# Revit family: Rohrschellen Form A, Typ TGA, Gummi
name_source: partatom
category: HLS-Bauteile
revit_build: Autodesk Revit 2017 (Build: 20190507_1515(x64)
units: mm (PartAtom-declared; Revit-internal decimal feet)

## family parameters
Arbeitsebenenbasiert = Ja
Beim Laden mit Abzugskörper schneiden = Nein
Bemaßung runder Anschluss = Durchmesser verwenden
Gemeinsam genutzt = Ja
Immer vertikal = Nein
Raumberechnungspunkt = Nein
Teiletyp = Normal

## types (17) — shared parameters
Anschluss = ohne Anschluss
Bauart = zweiteilig
Baustoffklasse = B2
DS = 8 mm  [stored 0.0262467 ft]
Fabrikat = MEFA
Firma = MEFA Befestigungs- und Montagesysteme GmbH
Material = Stahl
Mengeneinheit = St
Oberflaeche = galvanisch verzinkt
Rohraußendurchmesser Zoll = Zoll
Vorgabe-Ansicht = 1219 mm
max. Temperaturbeständigkeit = 100 °C
max. zul. Last horizontal = 0.00 kN
max. zul. Last vertikal = 0.00 kN
vpe = 1 St
zero-valued in all types: AB, HGA, Nennweite DN Rohr, Stärke Material, max. Rohraußendurchmesser, min. Rohraußendurchmesser

## per-type parameters (varying)
| type | A | Achsabstand | Artikelnummer | B | C | D | D0 | DF1 | DF2 | DVS | EAN | Gewicht | Gewicht pro Bauteil | H | Kurztext1 | Kurztext2 | MB | MD | Materialmaße | R | RM | Rohraußendurchmesser | S | Verschluss-Schraube |
| Rohrschellen Form A, Typ TGA, Ø 219, Gummi | 14 mm  [stored 0.0459318 ft] | 304 mm | 109gfba0219 | 357 mm | 24 mm  [stored 0.0787402 ft] | 219 mm  [stored 0.718504 ft] | 235 mm | 48 mm  [stored 0.15748 ft] | 45 mm  [stored 0.147638 ft] | 17 mm | 4250928423672 | 3.27 kg | 3.27 kg | 247 mm | Rohrschelle Form A TGA 60x6,0 | 219 mm ohne Anschluss TPE gvz | 60 mm  [stored 0.19685 ft] | 6 mm  [stored 0.019685 ft] | 60x6,0 mm | 118 mm | 124 mm | 219 mm  [stored 0.718504 ft] | 309 mm | M16 |
| Rohrschellen Form A, Typ TGA, Ø 267, Gummi | 14 mm  [stored 0.0459318 ft] | 353 mm | 109gfba0267 | 405 mm | 24 mm  [stored 0.0787402 ft] | 267 mm | 283 mm | 48 mm  [stored 0.15748 ft] | 45 mm  [stored 0.147638 ft] | 17 mm | 4250928423689 | 3.85 kg | 3.85 kg | 295 mm | Rohrschelle Form A TGA 60x6,0 | 267 mm ohne Anschluss TPE gvz | 60 mm  [stored 0.19685 ft] | 6 mm  [stored 0.019685 ft] | 60x6,0 mm | 142 mm | 148 mm | 267 mm | 357 mm | M16 |
| Rohrschellen Form A, Typ TGA, Ø 273, Gummi | 14 mm  [stored 0.0459318 ft] | 359 mm | 109gfba0273 | 411 mm | 24 mm  [stored 0.0787402 ft] | 273 mm | 289 mm | 48 mm  [stored 0.15748 ft] | 45 mm  [stored 0.147638 ft] | 17 mm | 4250928423696 | 3.92 kg | 3.92 kg | 301 mm | Rohrschelle Form A TGA 60x6,0 | 273 mm ohne Anschluss TPE gvz | 60 mm  [stored 0.19685 ft] | 6 mm  [stored 0.019685 ft] | 60x6,0 mm | 145 mm | 151 mm | 273 mm | 363 mm | M16 |
| Rohrschellen Form A, Typ TGA, Ø 356, Gummi | 16 mm  [stored 0.0524934 ft] | 446 mm | 109ggba0356 | 498 mm | 24 mm  [stored 0.0787402 ft] | 356 mm | 372 mm | 48 mm  [stored 0.15748 ft] | 45 mm  [stored 0.147638 ft] | 17 mm | 4250928423764 | 6.18 kg | 6.18 kg | 388 mm | Rohrschelle Form A TGA 60x8,0 | 356 mm ohne Anschluss TPE gvz | 60 mm  [stored 0.19685 ft] | 8 mm  [stored 0.0262467 ft] | 60x8,0 mm | 186 mm  [stored 0.610236 ft] | 194 mm | 356 mm | 450 mm | M16 |
| Rohrschellen Form A, Typ TGA, Ø 368, Gummi | 16 mm  [stored 0.0524934 ft] | 458 mm | 109ggba0368 | 510 mm | 24 mm  [stored 0.0787402 ft] | 368 mm | 384 mm | 48 mm  [stored 0.15748 ft] | 45 mm  [stored 0.147638 ft] | 17 mm | 4250928423771 | 6.36 kg | 6.36 kg | 400 mm | Rohrschelle Form A TGA 60x8,0 | 368 mm ohne Anschluss TPE gvz | 60 mm  [stored 0.19685 ft] | 8 mm  [stored 0.0262467 ft] | 60x8,0 mm | 192 mm  [stored 0.629921 ft] | 200 mm  [stored 0.656168 ft] | 368 mm | 462 mm | M16 |
| Rohrschellen Form A, Typ TGA, Ø 406, Gummi | 16 mm  [stored 0.0524934 ft] | 497 mm | 109ggba0406 | 548 mm | 24 mm  [stored 0.0787402 ft] | 406 mm | 422 mm | 48 mm  [stored 0.15748 ft] | 45 mm  [stored 0.147638 ft] | 17 mm | 4250928423788 | 6.93 kg | 6.93 kg | 438 mm | Rohrschelle Form A TGA 60x8,0 | 406 mm ohne Anschluss TPE gvz | 60 mm  [stored 0.19685 ft] | 8 mm  [stored 0.0262467 ft] | 60x8,0 mm | 211 mm  [stored 0.692257 ft] | 219 mm  [stored 0.718504 ft] | 406 mm | 500 mm | M16 |
| Rohrschellen Form A, Typ TGA, Ø 419, Gummi | 16 mm  [stored 0.0524934 ft] | 510 mm | 109ggba0419 | 561 mm | 24 mm  [stored 0.0787402 ft] | 419 mm | 435 mm | 48 mm  [stored 0.15748 ft] | 45 mm  [stored 0.147638 ft] | 17 mm | 4250928423795 | 7.13 kg | 7.13 kg | 451 mm | Rohrschelle Form A TGA 60x8,0 | 419 mm ohne Anschluss TPE gvz | 60 mm  [stored 0.19685 ft] | 8 mm  [stored 0.0262467 ft] | 60x8,0 mm | 218 mm | 226 mm | 419 mm | 513 mm | M16 |
| Rohrschellen Form A, Typ TGA, Ø 457, Gummi | 16 mm  [stored 0.0524934 ft] | 548 mm | 109ggba0457 | 599 mm | 24 mm  [stored 0.0787402 ft] | 457 mm | 473 mm | 48 mm  [stored 0.15748 ft] | 45 mm  [stored 0.147638 ft] | 17 mm | 4250928423801 | 7.69 kg | 7.69 kg | 489 mm | Rohrschelle Form A TGA 60x8,0 | 457 mm ohne Anschluss TPE gvz | 60 mm  [stored 0.19685 ft] | 8 mm  [stored 0.0262467 ft] | 60x8,0 mm | 237 mm | 245 mm | 457 mm | 551 mm | M16 |
| Rohrschellen Form A, Typ TGA, Ø 508, Gummi | 18 mm  [stored 0.0590551 ft] | 614 mm | 109ghba0508 | 679 mm | 30 mm  [stored 0.0984252 ft] | 508 mm | 524 mm | 60 mm  [stored 0.19685 ft] | 52 mm | 23 mm  [stored 0.0754593 ft] | 4250928423863 | 12.04 kg | 12.04 kg | 544 mm | Rohrschelle Form A TGA 70x10,0 | 508 mm ohne Anschluss TPE gvz | 70 mm  [stored 0.229659 ft] | 10 mm  [stored 0.0328084 ft] | 70x10,0 mm | 262 mm | 272 mm | 508 mm | 619 mm | M20 |
| Rohrschellen Form A, Typ TGA, Ø 521, Gummi | 18 mm  [stored 0.0590551 ft] | 627 mm | 109ghba0521 | 692 mm | 30 mm  [stored 0.0984252 ft] | 521 mm | 537 mm | 60 mm  [stored 0.19685 ft] | 52 mm | 23 mm  [stored 0.0754593 ft] | 4250928423870 | 12.31 kg | 12.31 kg | 557 mm | Rohrschelle Form A TGA 70x10,0 | 521 mm ohne Anschluss TPE gvz | 70 mm  [stored 0.229659 ft] | 10 mm  [stored 0.0328084 ft] | 70x10,0 mm | 269 mm | 279 mm | 521 mm | 632 mm | M20 |
| Rohrschellen Form A, Typ TGA, Ø 610, Gummi | 18 mm  [stored 0.0590551 ft] | 716 mm | 109ghba0610 | 781 mm | 30 mm  [stored 0.0984252 ft] | 610 mm | 626 mm | 60 mm  [stored 0.19685 ft] | 52 mm | 23 mm  [stored 0.0754593 ft] | 4250928423887 | 14.18 kg | 14.18 kg | 646 mm | Rohrschelle Form A TGA 70x10,0 | 610 mm ohne Anschluss TPE gvz | 70 mm  [stored 0.229659 ft] | 10 mm  [stored 0.0328084 ft] | 70x10,0 mm | 313 mm | 323 mm | 610 mm | 721 mm | M20 |
| Rohrschellen Form A, Typ TGA, Ø 711, Gummi | 18 mm  [stored 0.0590551 ft] | 818 mm | 109ghba0711 | 882 mm | 30 mm  [stored 0.0984252 ft] | 711 mm | 727 mm | 60 mm  [stored 0.19685 ft] | 52 mm | 23 mm  [stored 0.0754593 ft] | 4250928423894 | 16.29 kg | 16.29 kg | 747 mm | Rohrschelle Form A TGA 70x10,0 | 711 mm ohne Anschluss TPE gvz | 70 mm  [stored 0.229659 ft] | 10 mm  [stored 0.0328084 ft] | 70x10,0 mm | 364 mm | 374 mm | 711 mm | 822 mm | M20 |
| Rohrschellen Form A, Typ TGA, Ø 813, Gummi | 18 mm  [stored 0.0590551 ft] | 920 mm | 109ghba0813 | 984 mm | 30 mm  [stored 0.0984252 ft] | 813 mm | 829 mm | 60 mm  [stored 0.19685 ft] | 52 mm | 23 mm  [stored 0.0754593 ft] | 4250928423900 | 18.44 kg | 18.44 kg | 849 mm | Rohrschelle Form A TGA 70x10,0 | 813 mm ohne Anschluss TPE gvz | 70 mm  [stored 0.229659 ft] | 10 mm  [stored 0.0328084 ft] | 70x10,0 mm | 415 mm | 425 mm | 813 mm | 924 mm | M20 |
| Rohrschellen Form A, Typ TGA, Ø 914, Gummi | 23 mm  [stored 0.0754593 ft] | 1050 mm | 109gkba0914 | 1127 mm | 36 mm  [stored 0.11811 ft] | 914 mm | 930 mm | 72 mm  [stored 0.23622 ft] | 68 mm | 27 mm  [stored 0.0885827 ft] | 4250928423948 | 38.24 kg | 38.24 kg | 960 mm | Rohrschelle Form A TGA 90x15,0 | 914 mm ohne Anschluss TPE gvz | 90 mm  [stored 0.295276 ft] | 15 mm  [stored 0.0492126 ft] | 90x15,0 mm | 465 mm | 480 mm | 914 mm | 1055 mm | M24 |
| Rohrschellen Form A, Typ TGA, Ø1016, Gummi | 23 mm  [stored 0.0754593 ft] | 1153 mm | 109gkba1016 | 1229 mm | 36 mm  [stored 0.11811 ft] | 1016 mm | 1032 mm | 72 mm  [stored 0.23622 ft] | 68 mm | 27 mm  [stored 0.0885827 ft] | 4250928423955 | 42.24 kg | 42.24 kg | 1062 mm | Rohrschelle Form A TGA 90x15,0 | 1016 mm ohne Anschluss TPE gvz | 90 mm  [stored 0.295276 ft] | 15 mm  [stored 0.0492126 ft] | 90x15,0 mm | 516 mm | 531 mm | 1016 mm | 1157 mm | M24 |
| Rohrschellen Form A, Typ TGA, Ø1220, Gummi | 23 mm  [stored 0.0754593 ft] | 1357 mm | 109gkba1220 | 1433 mm | 36 mm  [stored 0.11811 ft] | 1220 mm | 1236 mm | 72 mm  [stored 0.23622 ft] | 68 mm | 27 mm  [stored 0.0885827 ft] | 4250928423962 | 50.25 kg | 50.25 kg | 1266 mm | Rohrschelle Form A TGA 90x15,0 | 1220 mm ohne Anschluss TPE gvz | 90 mm  [stored 0.295276 ft] | 15 mm  [stored 0.0492126 ft] | 90x15,0 mm | 618 mm | 633 mm | 1220 mm | 1361 mm | M24 |
| Rohrschellen Form A, Typ TGA, Ø 324, Gummi | 14 mm  [stored 0.0459318 ft] | 411 mm | 109gfba0324 | 462 mm | 24 mm  [stored 0.0787402 ft] | 324 mm | 340 mm | 48 mm  [stored 0.15748 ft] | 45 mm  [stored 0.147638 ft] | 17 mm | 4250928423702 | 4.54 kg | 4.54 kg | 352 mm | Rohrschelle Form A TGA 60x6,0 | 324 mm ohne Anschluss TPE gvz | 60 mm  [stored 0.19685 ft] | 6 mm  [stored 0.019685 ft] | 60x6,0 mm | 170 mm  [stored 0.557743 ft] | 176 mm  [stored 0.577428 ft] | 324 mm | 414 mm | M16 |

note: [stored X ft] marks values corroborated as IEEE doubles in the binary element streams (Revit-internal decimal feet)

## geometry (parser evidence)
native form markers: Sweep x2
no freeform markers — native parametric forms only
